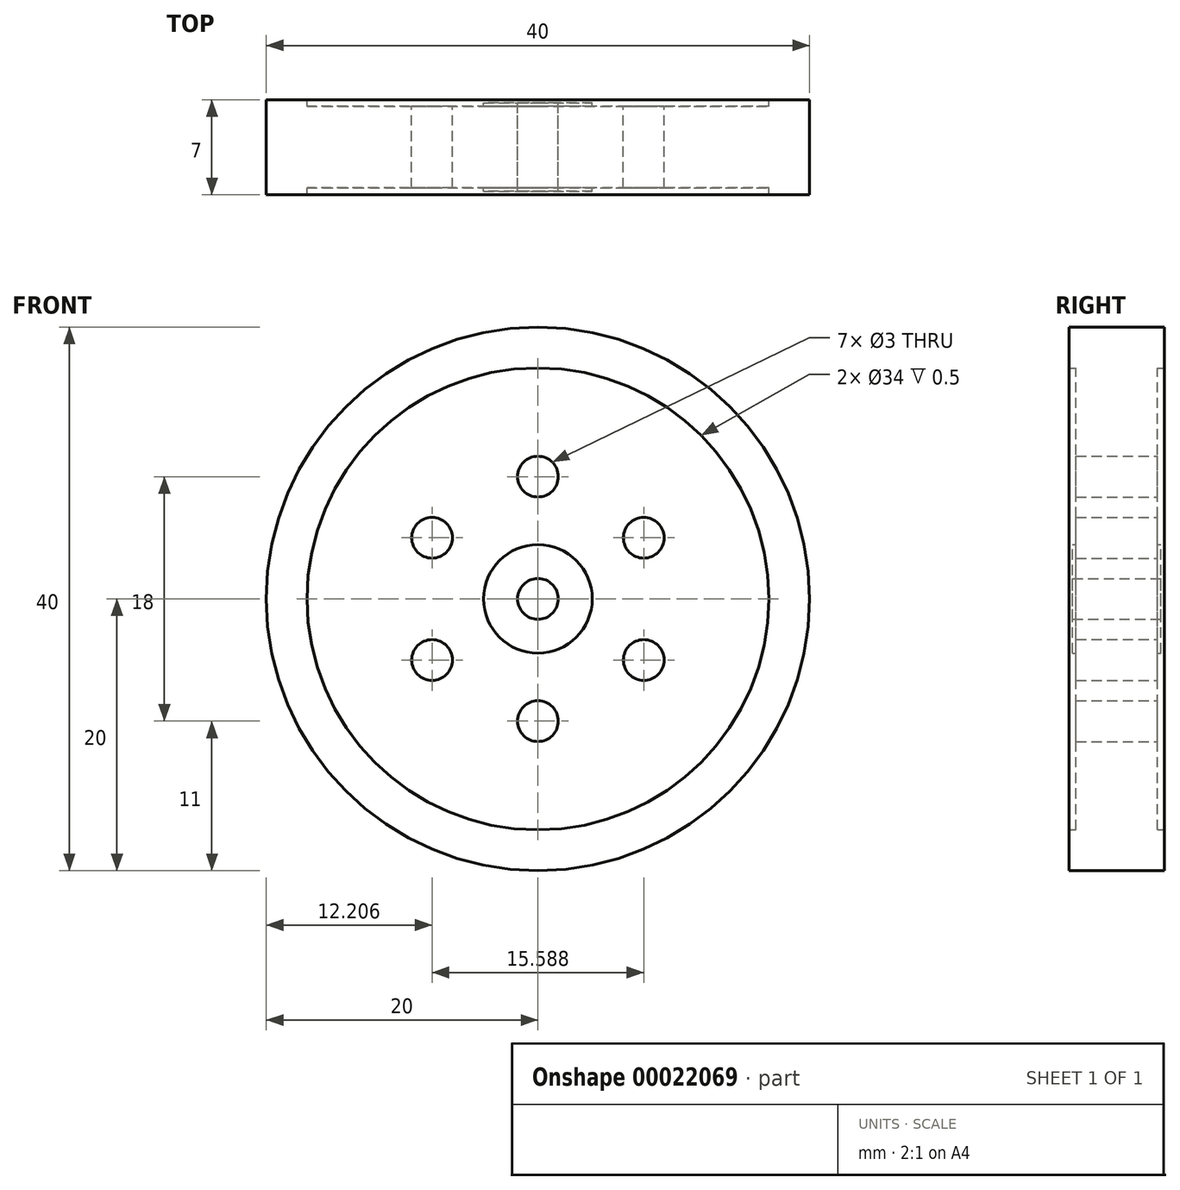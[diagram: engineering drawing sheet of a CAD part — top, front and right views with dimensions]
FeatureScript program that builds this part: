
annotation { "Feature Type Name" : "Feature", "Feature Type Description" : "" }
export const myFeature = defineFeature(function(context is Context, id is Id, definition is map)
    precondition{}
    {
        {
            var Q0;
            Q0=qCreatedBy(makeId("Front.planeOp"),FACE);
            var sketch = newSketch(context, id + "F0", { "sketchPlane" : qUnion([Q0])});
            skCircle(sketch, "E0", {"center": v(0, 0) * mm, "radius": 20 * mm});
            skCircle(sketch, "E1", {"center": v(0, 0) * mm, "radius": 4 * mm});
            skCircle(sketch, "E2", {"center": v(0, 0) * mm, "radius": 1.5 * mm});
            skCircle(sketch, "E3", {"center": v(0, 9) * mm, "radius": 1.5 * mm});
            skCircle(sketch, "E4.1.0", {"center": v(-7.8, 4.5) * mm, "radius": 1.5 * mm});
            skCircle(sketch, "E4.2.0", {"center": v(-7.8, -4.5) * mm, "radius": 1.5 * mm});
            skCircle(sketch, "E4.3.0", {"center": v(0, -9) * mm, "radius": 1.5 * mm});
            skCircle(sketch, "E4.4.0", {"center": v(7.8, -4.5) * mm, "radius": 1.5 * mm});
            skCircle(sketch, "E4.5.0", {"center": v(7.8, 4.5) * mm, "radius": 1.5 * mm});
            skCircle(sketch, "E5", {"center": v(0, 0) * mm, "radius": 17 * mm});
            skSolve(sketch);
        }
        {
            var Q0;
            Q0=makeQuery(id+"F0.imprint","IMPRINT",FACE,{"disambiguationData":[TD([[makeQuery(id+"F0.imprint","IMPRINT",EDGE,{"derivedFrom":sQuery(id+"F0.wireOp",EDGE,"E1")}),1.0]])]});
            extrude(context, id + "F1", {"entities" : qUnion([Q0]), "endBound" : BoundingType.SYMMETRIC, "depth" : 6.5 * mm});
        }
        {
            var Q0;
            Q0=makeQuery(id+"F0.imprint","IMPRINT",FACE,{"disambiguationData":[TD([[makeQuery(id+"F0.imprint","IMPRINT",EDGE,{"derivedFrom":sQuery(id+"F0.wireOp",EDGE,"E1")}),-1.0]])]});
            extrude(context, id + "F2", {"entities" : qUnion([Q0]), "operationType" : NewBodyOperationType.ADD, "endBound" : BoundingType.SYMMETRIC, "depth" : 6 * mm});
        }
        {
            var Q0;
            Q0 = qSketchRegion(id + "F0", true);
            extrude(context, id + "F3", {"entities" : qUnion([Q0]), "operationType" : NewBodyOperationType.ADD, "endBound" : BoundingType.SYMMETRIC, "depth" : 7 * mm});
        }
    });
